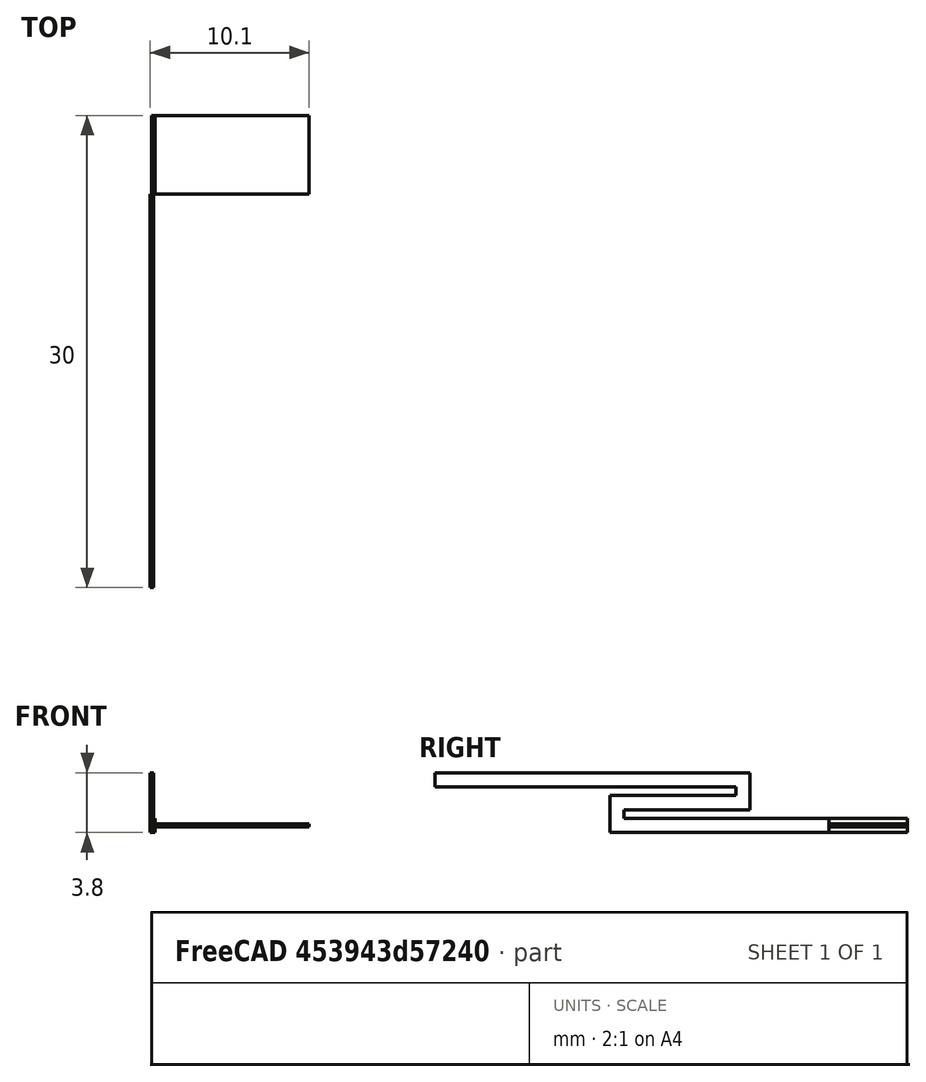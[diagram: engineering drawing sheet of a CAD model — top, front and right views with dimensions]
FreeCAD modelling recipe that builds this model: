
FCSTD DOCUMENT  (FreeCAD 0.19R24291 (Git))
Label: Spring_FEM_A2
License: All rights reserved
LicenseURL: http://en.wikipedia.org/wiki/All_rights_reserved
objects: Sketcher::SketchObject×3, PartDesign::Pad×2, Fem::ConstraintDisplacement×2, Fem::FemSolverObjectPython×1, App::MaterialObjectPython×1, PartDesign::Pocket×1, PartDesign::Body×1, Fem::ConstraintForce×1, Fem::FemMeshShapeNetgenObject×1, Fem::FemMeshObjectPython×1, Fem::FemResultObjectPython×1, Fem::FemAnalysis×1
note: 10 computed .brp shape members not serialized (recipe doc carries the construction recipe); baked Part::Feature solids carry a one-line shape summary decoded from their .brp

FEATURE [Sketcher::SketchObject] Sketch023
  FullyConstrained = true
  MapMode = 5
  Placement = pos=(0,0,0) rot=(0.57735,0.57735,0.57735;2.0944rad)
  Support = -> [YZ_Plane014]
  sketch-geometry (12):
    g0: LineSegment StartX=-26 StartY=1.9 StartZ=0 EndX=-26 EndY=1 EndZ=0
    g1: LineSegment StartX=-26 StartY=1 StartZ=0 EndX=-6.9 EndY=1 EndZ=0
    g2: LineSegment StartX=-6.9 StartY=1 StartZ=0 EndX=-6.9 EndY=0.45 EndZ=0
    g3: LineSegment StartX=-6.9 StartY=0.45 StartZ=0 EndX=-14.9 EndY=0.45 EndZ=0
    g4: LineSegment StartX=-14.9 StartY=0.45 StartZ=0 EndX=-14.9 EndY=-1.9 EndZ=0
    g5: LineSegment StartX=-14.9 StartY=-1.9 StartZ=0 EndX=-1 EndY=-1.9 EndZ=0
    g6: LineSegment StartX=-26 StartY=1.9 StartZ=0 EndX=-6 EndY=1.9 EndZ=0
    g7: LineSegment StartX=-6 StartY=1.9 StartZ=0 EndX=-6 EndY=-0.45 EndZ=0
    g8: LineSegment StartX=-6 StartY=-0.45 StartZ=0 EndX=-14 EndY=-0.45 EndZ=0
    g9: LineSegment StartX=-14 StartY=-0.45 StartZ=0 EndX=-14 EndY=-1 EndZ=0
    g10: LineSegment StartX=-14 StartY=-1 StartZ=0 EndX=-1 EndY=-1 EndZ=0
    g11: LineSegment StartX=-1 StartY=-1 StartZ=0 EndX=-1 EndY=-1.9 EndZ=0
  constraints (36):
    c: Vertical(g0)
    c: Coincident(g4,g5)
    c: Horizontal(g5)
    c: Coincident(g0,g6)
    c: Horizontal(g6)
    c: Coincident(g6,g7)
    c: Vertical(g7)
    c: Coincident(g7,g8)
    c: Horizontal(g8)
    c: Coincident(g8,g9)
    c: Vertical(g9)
    c: Coincident(g9,g10)
    c: Coincident(g10,g11)
    c: Coincident(g11,g5)
    c: Vertical(g11)
    c: DistanceY(g11,g11) = 0.9
    c: Horizontal(g10)
    c: Vertical(g2)
    c: DistanceY(g9,g9) = 0.55
    c: Vertical(g4)
    c: DistanceY(g4,g-1) = 1.9
    c: DistanceY(g-1,g0) = 1.9
    c: DistanceY(g0,g0) = 0.9
    c: DistanceY(g2,g2) = 0.55
    c: Coincident(g1,g2)
    c: Coincident(g2,g3)
    c: Coincident(g3,g4)
    c: Horizontal(g1)
    c: Horizontal(g3)
    c: Coincident(g0,g1)
    c: DistanceX(g6,g-1) = 6
    c: DistanceX(g1,g6) = 0.9
    c: DistanceX(g9,g-1) = 14
    c: DistanceX(g3,g8) = 0.9
    c: DistanceX(g0,g-1) = 26
    c: DistanceX(g10,g-1) = 1
FEATURE [PartDesign::Pad] Pad015
  Direction = (1,1,1)
  Length = 0.2
  Length2 = 100
  Midplane = true
  Placement = pos=(0,0,0) rot=(0.57735,0.57735,0.57735;2.0944rad)
  Profile = -> Sketch023
  Type = 0
FEATURE [Fem::FemSolverObjectPython] SolverCcxTools  # FEM object (typed FeaturePython)
  AnalysisType = 0
  BeamShellResultOutput3D = false
  EigenmodeHighLimit = 1000000
  EigenmodeLowLimit = 0
  EigenmodesCount = 10
  GeometricalNonlinearity = 0
  IterationsControlParameterCutb = 0.25,0.5,0.75,0.85,,,1.5,
  IterationsControlParameterIter = 4,8,9,200,10,400,,200,,
  IterationsControlParameterTimeUse = false
  IterationsThermoMechMaximum = 2000
  IterationsUserDefinedIncrementations = false
  IterationsUserDefinedTimeStepLength = false
  MaterialNonlinearity = 0
  MatrixSolverType = 0
  SplitInputWriter = false
  ThermoMechSteadyState = true
  TimeEnd = 1
  TimeInitialStep = 0.01
FEATURE [App::MaterialObjectPython] MaterialSolid  # material (typed FeaturePython)
  Category = 0
  Material = AuthorAndLicense=PLA-Generic,CardName=PLA-Generic,Density=1240 kg/m^3,+12 more (map truncated)
FEATURE [Fem::ConstraintDisplacement] ConstraintDisplacement
  NormalDirection = (-4e-16,-1,2e-16)
  Normals = (9) [(-4.4e-16,-1,2.2e-16),(-4.4e-16,-1,2.2e-16),(-4.4e-16,-1,2.2e-16),(-4.4e-16,-1,2.2e-16),(-4.4e-16,-1,2.2e-16),(-4.4e-16,-1,2.2e-16),+3 more]
  Points = (9) [(0.1,-26,1.9),(0.1,-26,1.45),(0.1,-26,1),(-3.31679e-15,-26,1.9),(-3.1225e-15,-26,1.45),(-2.91434e-15,-26,1),(-0.1,-26,1.9),(-0.1,-26,1.45),+1 more]
  References = -> [Pad015]
  rotxFix = false
  rotxFree = true
  rotyFix = false
  rotyFree = true
  rotzFix = false
  rotzFree = true
  xDisplacement = 0
  xFix = true
  xFree = false
  xRotation = 0
  yDisplacement = 0
  yFix = false
  yFree = true
  yRotation = 0
  zDisplacement = 0
  zFix = true
  zFree = false
  zRotation = 0
FEATURE [Sketcher::SketchObject] Sketch
  ExternalGeometry = -> [Pad015]
  FullyConstrained = true
  MapMode = 5
  Placement = pos=(-4e-16,-1,2e-16) rot=(0.57735,0.57735,0.57735;4.18879rad)
  Support = -> [Pad015]
  sketch-geometry (4):
    g0: LineSegment StartX=-1.9 StartY=10 StartZ=0 EndX=-1 EndY=10 EndZ=0
    g1: LineSegment StartX=-1 StartY=10 StartZ=0 EndX=-1 EndY=0 EndZ=0
    g2: LineSegment StartX=-1 StartY=0 StartZ=0 EndX=-1.9 EndY=0 EndZ=0
    g3: LineSegment StartX=-1.9 StartY=0 StartZ=0 EndX=-1.9 EndY=10 EndZ=0
  constraints (12):
    c: Coincident(g0,g1)
    c: Coincident(g1,g2)
    c: Coincident(g2,g3)
    c: Coincident(g3,g0)
    c: Horizontal(g0)
    c: Horizontal(g2)
    c: Vertical(g1)
    c: Vertical(g3)
    c: PointOnObject(g2,g-1)
    c: PointOnObject(g1,g-4)
    c: PointOnObject(g2,g-3)
    c: DistanceY(g1,g1) = 10
FEATURE [PartDesign::Pad] Pad
  BaseFeature = -> Pad015
  Direction = (1,1,1)
  Length = 5
  Length2 = 100
  Placement = pos=(0,0,0) rot=(0.57735,0.57735,0.57735;2.0944rad)
  Profile = -> Sketch
  Type = 0
FEATURE [Fem::ConstraintDisplacement] ConstraintDisplacement001  label="RotationAxis"
  NormalDirection = (0,0,1)
  Normals = (2) [(0,0,1),(0,0,1)]
  Points = (2) [(0,-1,-1),(0,-1,-1.9)]
  References = -> [Pad]
  rotxFix = true
  rotxFree = false
  rotyFix = true
  rotyFree = false
  rotzFix = false
  rotzFree = true
  xDisplacement = 0
  xFix = true
  xFree = false
  xRotation = 0
  yDisplacement = 0
  yFix = true
  yFree = false
  yRotation = 0
  zDisplacement = 0
  zFix = true
  zFree = false
  zRotation = 0
FEATURE [Sketcher::SketchObject] Sketch024
  ExternalGeometry = -> [Pad]
  FullyConstrained = false
  MapMode = 5
  Placement = pos=(1.8e-15,4,0) rot=(0.57735,0.57735,0.57735;4.18879rad)
  Support = -> [Pad]
  sketch-geometry (8):
    g0: LineSegment StartX=-1.35 StartY=10.2103 StartZ=0 EndX=-0.656196 EndY=10.2103 EndZ=0
    g1: LineSegment StartX=-0.656196 StartY=10.2103 StartZ=0 EndX=-0.656196 EndY=0.2 EndZ=0
    g2: LineSegment StartX=-0.656196 StartY=0.2 StartZ=0 EndX=-1.35 EndY=0.2 EndZ=0
    g3: LineSegment StartX=-1.35 StartY=0.2 StartZ=0 EndX=-1.35 EndY=10.2103 EndZ=0
    g4: LineSegment StartX=-2.54734 StartY=10.2467 StartZ=0 EndX=-1.55 EndY=10.2467 EndZ=0
    g5: LineSegment StartX=-1.55 StartY=10.2467 StartZ=0 EndX=-1.55 EndY=0.2 EndZ=0
    g6: LineSegment StartX=-1.55 StartY=0.2 StartZ=0 EndX=-2.54734 EndY=0.2 EndZ=0
    g7: LineSegment StartX=-2.54734 StartY=0.2 StartZ=0 EndX=-2.54734 EndY=10.2467 EndZ=0
  constraints (20):
    c: Coincident(g0,g1)
    c: Coincident(g1,g2)
    c: Coincident(g2,g3)
    c: Coincident(g3,g0)
    c: Horizontal(g0)
    c: Horizontal(g2)
    c: Vertical(g1)
    c: Vertical(g3)
    c: Coincident(g4,g5)
    c: Coincident(g5,g6)
    c: Coincident(g6,g7)
    c: Coincident(g7,g4)
    c: Horizontal(g4)
    c: Horizontal(g6)
    c: Vertical(g5)
    c: Vertical(g7)
    c: DistanceY(g-1,g2) = 0.2
    c: DistanceY(g-1,g5) = 0.2
    c: DistanceX(g-4,g5) = 0.35
    c: DistanceX(g2,g-3) = 0.35
FEATURE [PartDesign::Pocket] Pocket
  BaseFeature = -> Pad
  Length = 5
  Length2 = 100
  Placement = pos=(0,0,0) rot=(0.57735,0.57735,0.57735;2.0944rad)
  Profile = -> Sketch024
  Type = 0
FEATURE [PartDesign::Body] Body008  label="Spring"
  Group = -> [Sketch023,Pad015,Sketch,Pad,Sketch024,Pocket]
  Origin = -> Origin014
  Tip = -> Pocket
FEATURE [Fem::ConstraintForce] ConstraintForce
  Direction = -> Pocket [Edge57]
  DirectionVector = (-6e-16,-1,5e-16)
  Force = 0.005
  NormalDirection = (1,-4e-16,4e-16)
  Points = (9) [(10,4,-1.55),(10,4,-1.45),(10,4,-1.35),(10,1.5,-1.55),(10,1.5,-1.45),(10,1.5,-1.35),(10,-1,-1.55),(10,-1,-1.45),(10,-1,-1.35)]
  References = -> [Pocket]
FEATURE [Fem::FemMeshShapeNetgenObject] FEMMeshNetgen
  Fineness = 2
  GrowthRate = 0.3
  MaxSize = 1
  NbSegsPerEdge = 1
  NbSegsPerRadius = 2
  Optimize = true
  SecondOrder = true
  Shape = -> Pocket
FEATURE [Fem::FemMeshObjectPython] ResultMesh  # FEM object (typed FeaturePython)
FEATURE [Fem::FemResultObjectPython] CCX_Results  # FEM object (typed FeaturePython)
  DisplacementLengths = [1.74828,3.90667,3.90664,1.74824,1.74817,1.7468,1.74698,1.74835,0.0689631,0.0691557,3.4943,3.49429,0.0691313,0.0688343,0,0,2.37699,2.82366,2.83048,0.0341981,0.0342905,2.95177,2.90851,2.36894,2.37699,2.82368,2.83045,0.0339134,0.033927,+2615 more]
  DisplacementVectors = (2644) [(1.74691,-0.0692616,-0.000390459),(1.74697,-3.4943,0.00155004),(1.74693,-3.49429,0.00155004),(1.74687,-0.0692452,-0.000390371),+2640 more]
  Eigenmode = 0
  EigenmodeFrequency = 0
  MaxShear = [0.00132434,0.0033595,0.00352819,0.00117524,0.000462744,0.000534978,0.00051515,0.000353272,2.43664,1.39026,0.00300271,0.00347076,2.10144,2.61319,3.92124,4.85739,0.463316,2.33261,2.29591,4.28675,4.14305,0.341873,0.24016,4.3167,0.29208,+2619 more]
  Mesh = -> ResultMesh
  NodeNumbers = [1,2,3,4,5,6,7,8,9,10,11,12,13,14,15,16,17,18,19,20,21,22,23,24,25,26,27,28,29,30,31,32,33,34,35,36,37,38,39,40,41,42,43,44,45,46,47,48,49,50,51,52,53,54,55,56,57,58,59,60,61,62,63,64,65,66,67,68,69,+2575 more]
  NodeStrainXX = [-3.70071e-07,8.66328e-07,9.11545e-07,-2.9259e-07,-1.32543e-07,5.06388e-08,1.93577e-08,-5.3753e-08,0.000427688,-0.000161506,-7.78001e-07,-9.99305e-07,-0.000214242,0.000459154,-0.000650077,-0.000555158,-8.34125e-05,-0.000278823,0.000349104,+2625 more]
  NodeStrainXY = [-2.54905e-08,-9.13543e-07,-9.42842e-07,-1.34865e-07,9.67452e-08,-9.10396e-08,-1.20769e-07,6.15575e-08,-0.000342452,-0.000467151,-8.24912e-07,-8.4323e-07,-0.000645632,-0.000358759,0.000886423,0.00141414,-4.80497e-05,-3.15275e-05,6.33611e-06,+2625 more]
  NodeStrainXZ = [-8.10138e-08,-4.88419e-08,4.94259e-08,-4.52757e-08,-3.62357e-08,5.03935e-08,-3.95502e-09,2.63606e-08,-0.000159579,-8.74136e-05,7.35105e-08,5.66159e-08,0.000220699,0.000184144,0.000325038,-0.000430095,-3.92513e-05,-0.000105024,-0.000119573,+2625 more]
  NodeStrainYY = [2.29319e-08,-8.5102e-07,-9.25736e-07,2.17678e-08,7.63017e-08,-7.91264e-08,-4.57279e-08,1.59824e-07,-0.00113808,-0.000405875,7.0355e-07,9.67876e-07,-0.000584018,-0.00121674,0.00151642,0.00148473,0.000136906,0.000896708,-0.000819011,+2625 more]
  NodeStrainYZ = [2.8157e-07,3.62239e-08,-4.93682e-08,-2.62643e-07,-7.44787e-08,1.76324e-07,-1.42808e-07,4.71834e-08,-3.63692e-05,-4.98947e-05,1.5544e-07,9.3403e-10,0.000236609,7.30769e-05,-0.000194938,0.000134124,0.000149395,0.000586172,0.000667417,+2625 more]
  NodeStrainZZ = [4.68289e-07,-1.12097e-08,-9.83326e-09,3.63359e-07,6.30121e-08,-6.10275e-08,-7.28982e-08,-2.63737e-08,0.000402341,0.000232155,1.52768e-08,3.02562e-08,0.00035402,0.000425808,-1.04302e-05,-7.30964e-06,4.2805e-06,-0.000358196,0.000169574,+2625 more]
  NodeStressXX = [-0.000573589,0.0023328,0.00235705,-0.000464671,-0.000331447,-0.000172504,-0.00028979,0.000130385,0.0846307,-1.58584,-0.00228593,-0.00267864,-2.10212,0.0872179,1.20543,1.68781,-0.0244409,0.147376,-0.0991294,-1.06185,-0.776668,-0.0897064,+2622 more]
  NodeStressXY = [-6.82247e-05,-0.00244507,-0.00252349,-0.000360963,0.000258936,-0.000243665,-0.000323235,0.000164757,-0.916562,-1.25032,-0.00220785,-0.00225688,-1.72802,-0.960208,2.37249,3.7849,-0.128604,-0.0843825,0.0169584,-2.50494,-2.56924,-0.0484444,+2622 more]
  NodeStressXZ = [-0.000216831,-0.000130724,0.000132287,-0.000121179,-9.69839e-05,0.000134877,-1.05855e-05,7.05532e-05,-0.427109,-0.23396,0.000196749,0.000151531,0.590694,0.492855,0.869955,-1.15114,-0.105055,-0.281095,-0.320033,0.758264,-0.845764,0.147038,+2622 more]
  NodeStressYY = [0.000478273,-0.00226363,-0.00256038,0.000376698,0.000227519,-0.000519817,-0.00046399,0.000702018,-4.10611,-2.23988,0.0016794,0.00258646,-3.09181,-4.39825,7.004,7.14751,0.565235,3.29365,-3.22555,-7.46141,-6.74197,-0.326167,0.316974,6.12358,+2620 more]
  NodeStressYZ = [0.000753614,9.69523e-05,-0.000132133,-0.000702957,-0.00019934,0.000471926,-0.000382223,0.000126285,-0.0973412,-0.133542,0.00041603,2.4999e-06,0.633278,0.195588,-0.521746,0.358978,0.399852,1.56887,1.78632,-0.722164,0.58612,0.260053,0.216331,+2621 more]
  NodeStressZZ = [0.00167026,-1.58994e-05,-0.00010899,0.00129096,0.00019195,-0.000471376,-0.00053671,0.000203665,0.0167888,-0.532214,-0.000162741,7.69471e-05,-0.581184,-0.00203067,2.91743,3.15411,0.210267,-0.0650654,-0.579635,-1.98477,-1.90537,-0.0131685,+2622 more]
  PrincipalMax = [0.00205432,0.00339756,0.00343007,0.00167445,0.00049198,1.86785e-05,6.33154e-05,0.000780314,0.567688,-0.447699,0.00269582,0.0034222,-0.377154,0.612755,7.85921,9.09155,0.856183,3.92123,0.46005,0.217914,0.578673,0.17772,0.508729,7.28778,+2620 more]
  PrincipalMed = [0.000114993,-2.28398e-05,-0.000116064,0.000204583,2.95506e-05,-0.000131098,-0.000386822,0.000181986,-0.266788,-0.682022,-0.000155486,8.18775e-05,-0.817921,-0.312185,3.25092,3.52111,-0.0346734,0.198705,-0.232595,-2.37036,-2.29525,-0.100735,+2622 more]
  PrincipalMin = [-0.000594369,-0.00332145,-0.00362632,-0.000676041,-0.000433509,-0.00105128,-0.000966984,7.37688e-05,-4.30559,-3.22821,-0.00330961,-0.00351931,-4.58004,-4.61363,0.0167267,-0.623228,-0.0704484,-0.743978,-4.13177,-8.35559,-7.70743,-0.506027,+2622 more]
  ResultType = Fem::ResultMechanical
  Stats = [-2.95175,1.74698,-3.4943,0.0339268,-0.00151317,0.0022133,0,3.90667,0.000262053,9.52504,-1.21201,11.9158,-3.0204,5.26036,-11.2914,2.09062,0.000148174,5.48763,0,0,0,0,0,0,0,0]
  Time = 0
  vonMises = [0.00237484,0.00581915,0.00611104,0.00205679,0.000801497,0.00100349,0.00089463,0.000659133,4.51426,2.67107,0.00520306,0.00601295,4.00075,4.83079,6.82645,8.44341,0.909272,4.27259,4.28767,7.61666,7.28734,0.595528,0.475412,7.88203,0.525207,+2619 more]
FEATURE [Fem::FemAnalysis] Analysis
  Group = -> [SolverCcxTools,MaterialSolid,ConstraintDisplacement,ConstraintDisplacement001,ConstraintForce,FEMMeshNetgen,CCX_Results]
